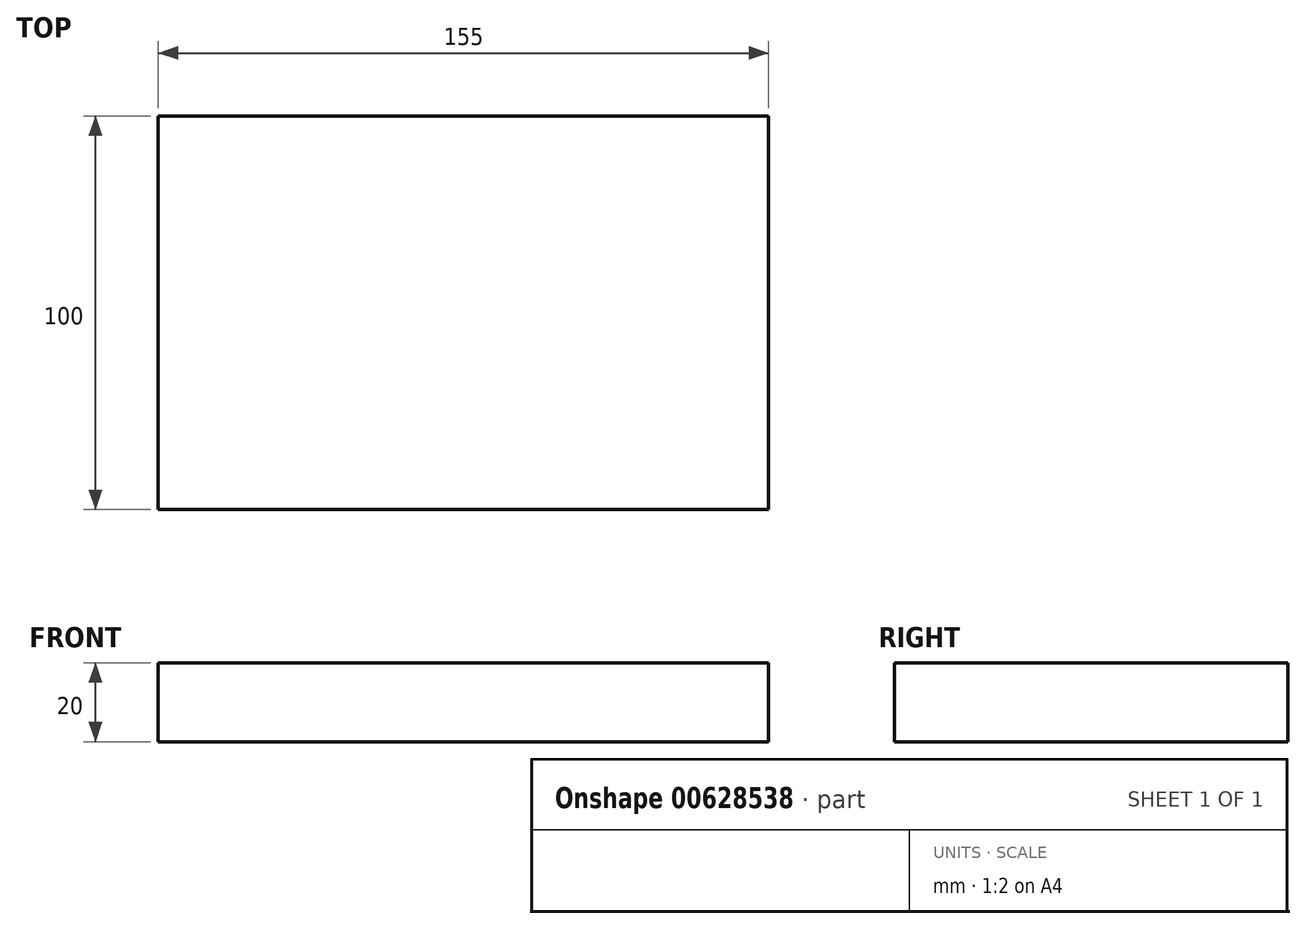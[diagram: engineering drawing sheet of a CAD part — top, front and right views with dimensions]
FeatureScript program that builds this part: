
annotation { "Feature Type Name" : "Feature", "Feature Type Description" : "" }
export const myFeature = defineFeature(function(context is Context, id is Id, definition is map)
    precondition{}
    {
        {
            var Q0;
            Q0=qCreatedBy(makeId("Top.planeOp"),FACE);
            var sketch = newSketch(context, id + "F0", { "sketchPlane" : qUnion([Q0])});
            skLineSegment(sketch, "E0.bottom", {"start": v(77.5, 50) * mm, "end": v(-77.5, 50) * mm});
            skLineSegment(sketch, "E0.top", {"start": v(77.5, -50) * mm, "end": v(-77.5, -50) * mm});
            skLineSegment(sketch, "E0.left", {"start": v(77.5, 50) * mm, "end": v(77.5, -50) * mm});
            skLineSegment(sketch, "E0.right", {"start": v(-77.5, 50) * mm, "end": v(-77.5, -50) * mm});
            skPoint(sketch, "E0.middle", {"position": v(0, 0) * mm});
            skSolve(sketch);
        }
        {
            var Q0;
            Q0 = qSketchRegion(id + "F0", true);
            extrude(context, id + "F1", {"entities" : qUnion([Q0]), "depth" : 20 * mm, "offsetDistance" : 25 * mm});
        }
    });
